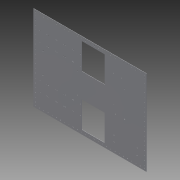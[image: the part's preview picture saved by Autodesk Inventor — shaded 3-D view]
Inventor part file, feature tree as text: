
AUTODESK INVENTOR PART (.ipt)
format: ipt  version: 2014 SP1 (Build 180222100, 222)  size: 347,136 bytes
history: native  units: in
note: dims shown in document units (in); Inventor stores cm internally (conversion verified against a paired STEP export)
features: reference x39, sketch x5, other x5, pattern_linear x2, sheet_metal_op x1
ambient origin geometry x8: Origin, YZ Plane, XZ Plane, XY Plane, X Axis, Y Axis, Z Axis, Center Point
bodies: Solid1 (feature_tree)
feature tree (52):
  sheet_metal_op  "Face1"
  pattern_linear  "Rectangular Pattern2"  Spacing1=7.25in  [1 undecoded]
  pattern_linear  "Rectangular Pattern5"  Spacing1=0.0625in  [1 undecoded]
  sketch  "Sketch1"  dims[d0=27.0in]
  other  "Plate1"
  sketch  "Sketch2"  dims[d1=20.325in]
  sketch  "Sketch4"  dims[d2=0.0625in]
  reference  "Reference4"
  reference  "Reference5"
  sketch  "Sketch12"  dims[d4=7.25in]
  reference  "Reference10"
  reference  "Reference11"
  sketch  "Sketch16"  dims[d5=5.5in d6=7.25in d17=0.0625in d18=0.0in d19=10.6299in d21=1.0in d23=1.0in d24=1.0in d65=0.0625in d66=0.0in d78=11.55in d79=5.5in d80=11.55in d97=0.0625in d98=0.0in d99=7.4803in d101=1.0in d102=0.7874in d104=26.0in d105=0.0625in d106=0.0in]
  reference  "Reference12"
  reference  "Reference13"
  reference  "Reference14"
  reference  "Reference15"
  reference  "Reference16"
  reference  "Reference17"
  reference  "Reference18"
  reference  "Reference19"
  reference  "Reference20"
  reference  "Reference21"
  reference  "Reference22"
  reference  "Reference23"
  reference  "Reference24"
  reference  "Reference25"
  reference  "Reference26"
  reference  "Reference27"
  reference  "Reference28"
  reference  "Reference29"
  reference  "Reference30"
  reference  "Reference31"
  reference  "Reference32"
  reference  "Reference33"
  reference  "Reference34"
  reference  "Reference35"
  reference  "Reference36"
  reference  "Reference37"
  reference  "Reference38"
  reference  "Reference39"
  reference  "Reference40"
  reference  "Reference41"
  reference  "Reference42"
  reference  "Reference43"
  reference  "Reference44"
  reference  "Reference45"
  reference  "Reference46"
  other  "Cut3"
  other  "Cut6"
  other  "Cut8"
  other  "Cut9"
note: 2 required parameter values undecoded (feature->parameter linkage not recoverable at this tier; creation-order binding heuristic only, values carry confidence <= 0.55)
